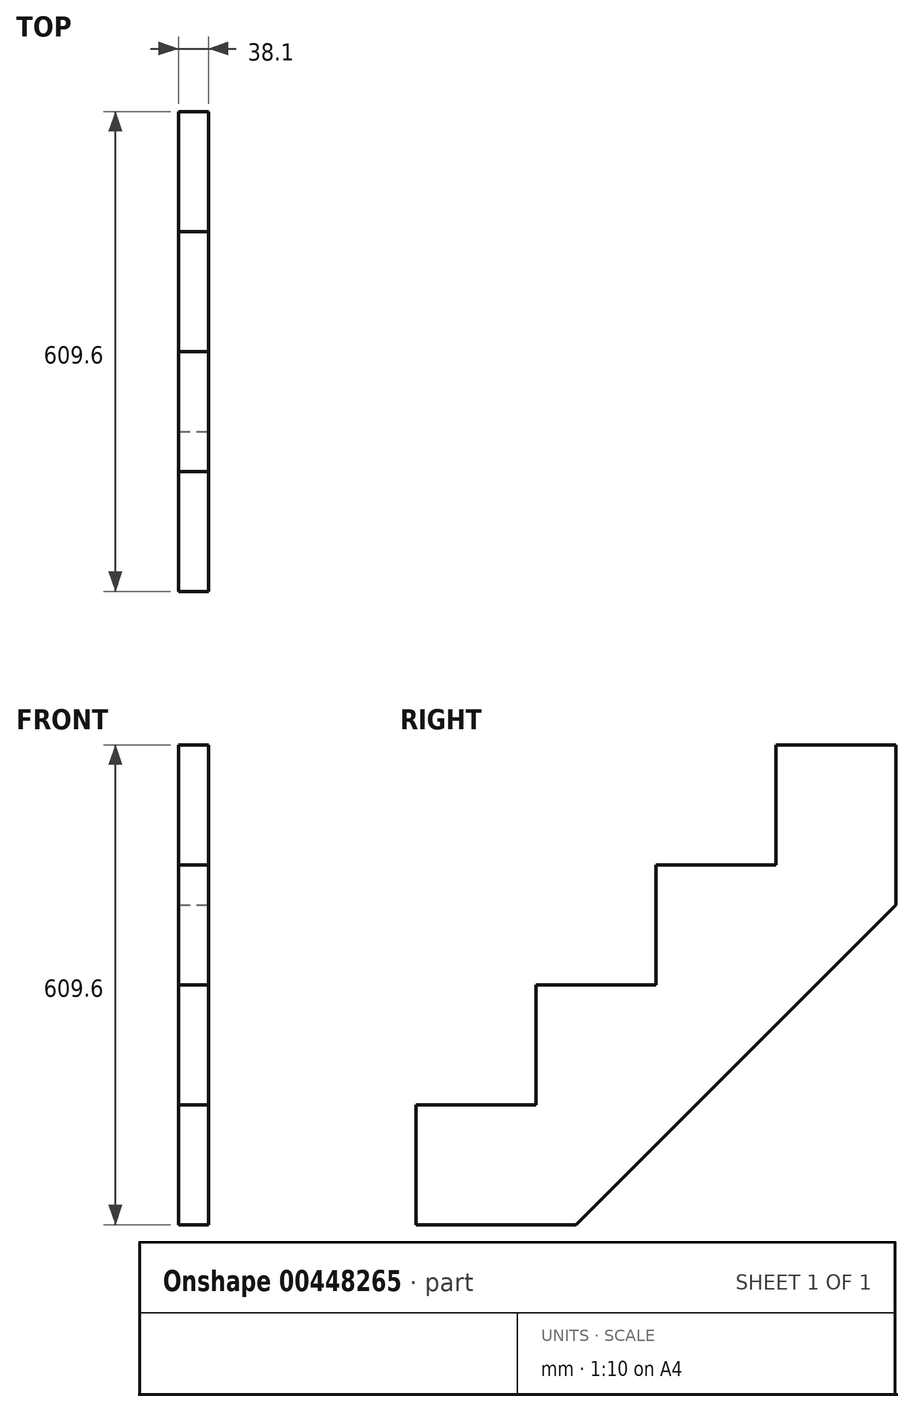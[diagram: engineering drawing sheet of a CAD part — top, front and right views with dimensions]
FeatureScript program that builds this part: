
annotation { "Feature Type Name" : "Feature", "Feature Type Description" : "" }
export const myFeature = defineFeature(function(context is Context, id is Id, definition is map)
    precondition{}
    {
        {
            var Q0;
            Q0=qCreatedBy(makeId("Right.planeOp"),FACE);
            var sketch = newSketch(context, id + "F0", { "sketchPlane" : qUnion([Q0])});
            skLineSegment(sketch, "E0", {"start": v(-457.2, -457.2) * mm, "end": v(-457.2, -304.8) * mm});
            skLineSegment(sketch, "E1", {"start": v(-457.2, -304.8) * mm, "end": v(-304.8, -304.8) * mm});
            skLineSegment(sketch, "E2", {"start": v(-304.8, -304.8) * mm, "end": v(-304.8, -152.4) * mm});
            skLineSegment(sketch, "E3", {"start": v(-304.8, -152.4) * mm, "end": v(-152.4, -152.4) * mm});
            skLineSegment(sketch, "E4", {"start": v(-152.4, -152.4) * mm, "end": v(-152.4, 0) * mm});
            skLineSegment(sketch, "E5", {"start": v(-152.4, 0) * mm, "end": v(0, 0) * mm});
            skLineSegment(sketch, "E6", {"start": v(0, 0) * mm, "end": v(0, -203.2) * mm});
            skLineSegment(sketch, "E7", {"start": v(0, -203.2) * mm, "end": v(-406.4, -609.6) * mm});
            skLineSegment(sketch, "E8", {"start": v(-457.2, -457.2) * mm, "end": v(-609.6, -457.2) * mm});
            skLineSegment(sketch, "E9", {"start": v(-609.6, -457.2) * mm, "end": v(-609.6, -609.6) * mm});
            skLineSegment(sketch, "E10", {"start": v(-609.6, -609.6) * mm, "end": v(-406.4, -609.6) * mm});
            skSolve(sketch);
        }
        {
            var Q0;
            Q0=makeQuery(id+"F0.imprint","IMPRINT",FACE,{"disambiguationData":[TD([[makeQuery(id+"F0.imprint","IMPRINT",EDGE,{"derivedFrom":sQuery(id+"F0.wireOp",EDGE,"E0")}),-1.0]])]});
            extrude(context, id + "F1", {"entities" : qUnion([Q0]), "oppositeDirection" : true, "depth" : 38.1 * mm});
        }
    });
